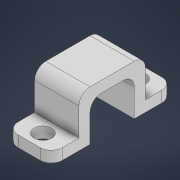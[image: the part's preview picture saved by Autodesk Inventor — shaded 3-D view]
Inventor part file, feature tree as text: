
AUTODESK INVENTOR PART (.ipt)
format: ipt  version: 2021 (Build 250183000, 183)  size: 161,792 bytes
history: native  units: mm
features: extrude x4, sketch x4, fillet x1
ambient origin geometry x8: Origin, YZ Plane, XZ Plane, XY Plane, X Axis, Y Axis, Z Axis, Center Point
bodies: Volumenkörper1 (feature_tree)
feature tree (9):
  extrude  "Extrusion1"  Depth=12.0mm
  extrude  "Extrusion2"  Depth=2.0mm
  extrude  "Extrusion3"  Depth=7.0mm TaperAngle=0.0deg
  extrude  "Extrusion4"  Depth=2.0mm
  fillet  "Rundung1"  Radius=5.0mm
  sketch  "Skizze1"  dims[d0=8.0mm d1=12.0mm]
  sketch  "Skizze2"  dims[d2=2.0mm d3=0.0mm d4=2.0mm]
  sketch  "Skizze3"  dims[d5=2.0mm d6=7.0mm d7=0.0mm]
  sketch  "Skizze4"  dims[d8=5.0mm d9=2.0mm d10=5.0mm d11=2.0mm d12=8.0mm d13=0.0mm d14=3.2mm d15=4.0mm d16=2.5mm d17=3.2mm d18=4.0mm d19=2.5mm d20=8.0mm d21=0.0mm d22=2.0mm]
